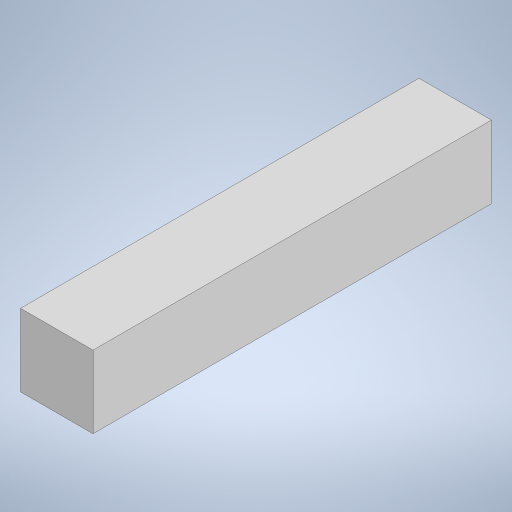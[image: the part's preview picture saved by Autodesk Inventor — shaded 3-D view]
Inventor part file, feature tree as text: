
AUTODESK INVENTOR PART (.ipt)
format: ipt  version: 2023 (Build 270158000, 158)  size: 205,312 bytes
history: native  units: mm
features: other x1, extrude x1, sketch x1
ambient origin geometry x8: Origin, YZ Plane, XZ Plane, XY Plane, X Axis, Y Axis, Z Axis, Center Point
bodies: Body1 (feature_tree)
feature tree (3):
  other  "Sólido1"
  extrude  "Extrusión1"  Depth=16.5mm
  sketch  "Boceto1"  dims[d0=3.0mm d1=16.5mm d2=3.0mm d3=0.0mm]
